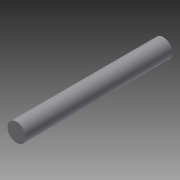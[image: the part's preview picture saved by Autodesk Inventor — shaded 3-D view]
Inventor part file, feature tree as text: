
AUTODESK INVENTOR PART (.ipt)
format: ipt  version: 2013 (Build 170138000, 138)  size: 67,584 bytes
history: native  units: in
note: dims shown in document units (in); Inventor stores cm internally (conversion verified against a paired STEP export)
features: extrude x1, sketch x1
ambient origin geometry x8: Origin, YZ Plane, XZ Plane, XY Plane, X Axis, Y Axis, Z Axis, Center Point
bodies: Solid1 (feature_tree)
feature tree (2):
  extrude  "Extrusion1"  Depth=1.5in TaperAngle=0.0deg
  sketch  "Sketch1"  dims[d0=0.1875in d3=1.5in d4=0.0in]
